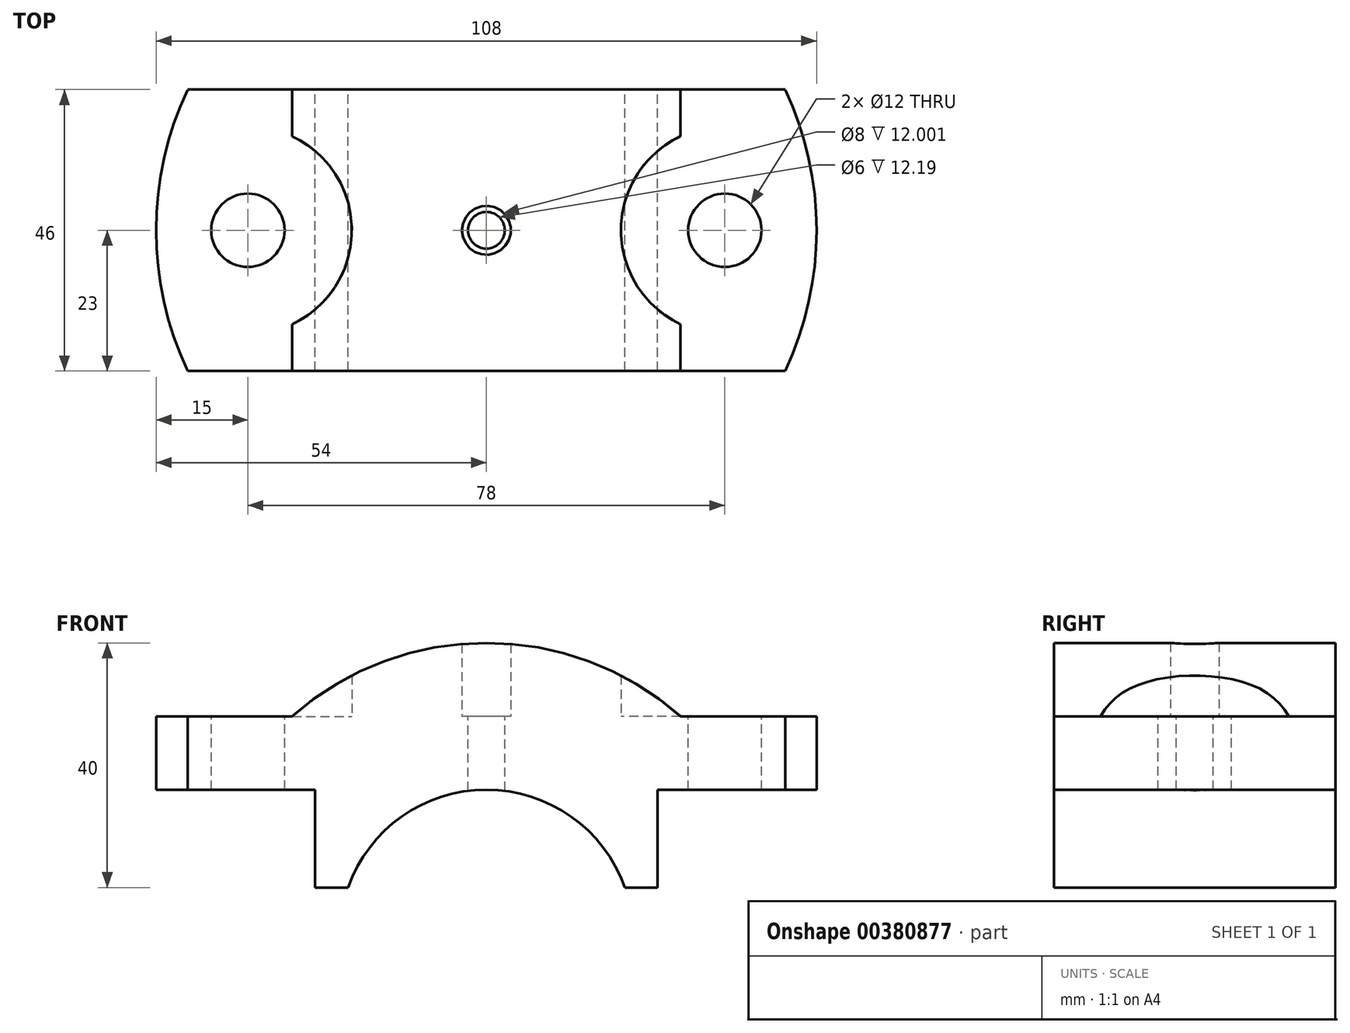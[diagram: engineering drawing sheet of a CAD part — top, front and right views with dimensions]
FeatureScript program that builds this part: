
annotation { "Feature Type Name" : "Feature", "Feature Type Description" : "" }
export const myFeature = defineFeature(function(context is Context, id is Id, definition is map)
    precondition{}
    {
        {
            var Q0;
            Q0=qCreatedBy(makeId("Front.planeOp"),FACE);
            var sketch = newSketch(context, id + "F0", { "sketchPlane" : qUnion([Q0])});
            skLineSegment(sketch, "E0.bottom", {"start": v(-54, 0) * mm, "end": v(54, 0) * mm});
            skLineSegment(sketch, "E0.top", {"start": v(-54, 12) * mm, "end": v(54, 12) * mm});
            skLineSegment(sketch, "E0.left", {"start": v(-54, 0) * mm, "end": v(-54, 12) * mm});
            skLineSegment(sketch, "E0.right", {"start": v(54, 0) * mm, "end": v(54, 12) * mm});
            skSolve(sketch);
        }
        {
            var Q0;
            Q0 = qSketchRegion(id + "F0", true);
            extrude(context, id + "F1", {"entities" : qUnion([Q0]), "endBound" : BoundingType.SYMMETRIC, "depth" : 46 * mm});
        }
        {
            var Q0;
            Q0=qCreatedBy(makeId("Front.planeOp"),FACE);
            var sketch = newSketch(context, id + "F2", { "sketchPlane" : qUnion([Q0])});
            skLineSegment(sketch, "E1", {"start": v(28, 0) * mm, "end": v(28, -16) * mm});
            skLineSegment(sketch, "E2", {"start": v(-28, 0) * mm, "end": v(-28, -16) * mm});
            skArc(sketch, "E3", {"start": v(22.63, -16) * mm, "mid": v(0, 0) * mm, "end": v(-22.63, -16) * mm});
            skLineSegment(sketch, "E4", {"start": v(-28, 0) * mm, "end": v(28, 0) * mm});
            skLineSegment(sketch, "E5", {"start": v(-22.63, -16) * mm, "end": v(-28, -16) * mm});
            skLineSegment(sketch, "E6", {"start": v(22.63, -16) * mm, "end": v(28, -16) * mm});
            skSolve(sketch);
        }
        {
            var Q0;
            Q0 = qSketchRegion(id + "F2", true);
            extrude(context, id + "F3", {"entities" : qUnion([Q0]), "operationType" : NewBodyOperationType.ADD, "endBound" : BoundingType.SYMMETRIC, "depth" : 46 * mm});
        }
        {
            var Q0;
            Q0=qCreatedBy(makeId("Front.planeOp"),FACE);
            var sketch = newSketch(context, id + "F4", { "sketchPlane" : qUnion([Q0])});
            skLineSegment(sketch, "E7.0", {"start": v(-54, 12) * mm, "end": v(54, 12) * mm});
            skArc(sketch, "E8", {"start": v(31.75, 12) * mm, "mid": v(0, 24) * mm, "end": v(-31.75, 12) * mm});
            skSolve(sketch);
        }
        {
            var Q0;
            Q0 = qSketchRegion(id + "F4", true);
            extrude(context, id + "F5", {"entities" : qUnion([Q0]), "operationType" : NewBodyOperationType.ADD, "endBound" : BoundingType.SYMMETRIC, "depth" : 46 * mm});
        }
        {
            var Q0;
            Q0=qCreatedBy(makeId("Top.planeOp"),FACE);
            var sketch = newSketch(context, id + "F6", { "sketchPlane" : qUnion([Q0])});
            skCircle(sketch, "E9", {"center": v(-39, 0) * mm, "radius": 6 * mm});
            skCircle(sketch, "E10", {"center": v(39, 0) * mm, "radius": 6 * mm});
            skSolve(sketch);
        }
        {
            var Q0;
            Q0 = qSketchRegion(id + "F6", true);
            extrude(context, id + "F7", {"entities" : qUnion([Q0]), "operationType" : NewBodyOperationType.REMOVE, "endBound" : BoundingType.THROUGH_ALL, "oppositeDirection" : true, "depth" : 25 * mm, "hasSecondDirection" : true, "secondDirectionOppositeDirection" : false, "secondDirectionDepth" : 25 * mm});
        }
        {
            var Q0;
            {var subQ4=sQuery(id+"F0.wireOp",EDGE,"E0.right");var subQ6=sQuery(id+"F0.wireOp",EDGE,"E0.top");Q0=makeQuery(id+"F5.boolean.opBoolean","SPLIT",FACE,{"disambiguationData":[TD([makeQuery(id+"F1.opExtrude","SWEPT_FACE",FACE,{"disambiguationData":[OSD([subQ4])]})])],"derivedFrom":makeQuery(id+"F1.opExtrude","SWEPT_FACE",FACE,{"disambiguationData":[OSD([subQ6])]})});}
            var sketch = newSketch(context, id + "F8", { "sketchPlane" : qUnion([Q0])});
            skLineSegment(sketch, "E11.0", {"start": v(31.75, -23) * mm, "end": v(31.75, 23) * mm});
            skLineSegment(sketch, "E12.0", {"start": v(-31.75, -23) * mm, "end": v(-31.75, 23) * mm});
            skArc(sketch, "E13", {"start": v(-31.75, -15.38) * mm, "mid": v(-22, 0) * mm, "end": v(-31.75, 15.38) * mm});
            skArc(sketch, "E14", {"start": v(31.75, 15.38) * mm, "mid": v(22, 0) * mm, "end": v(31.75, -15.38) * mm});
            skSolve(sketch);
        }
        {
            var Q0;
            Q0 = qSketchRegion(id + "F8", true);
            extrude(context, id + "F9", {"entities" : qUnion([Q0]), "operationType" : NewBodyOperationType.REMOVE, "depth" : 25 * mm});
        }
        {
            var Q0;
            {var subQ4=sQuery(id+"F0.wireOp",EDGE,"E0.right");var subQ6=sQuery(id+"F0.wireOp",EDGE,"E0.top");Q0=makeQuery(id+"F9.boolean.opBoolean","MERGE",FACE,{"derivedFrom":[makeQuery(id+"F5.boolean.opBoolean","SPLIT",FACE,{"disambiguationData":[TD([makeQuery(id+"F1.opExtrude","SWEPT_FACE",FACE,{"disambiguationData":[OSD([subQ4])]})])],"derivedFrom":makeQuery(id+"F1.opExtrude","SWEPT_FACE",FACE,{"disambiguationData":[OSD([subQ6])]})}),makeQuery(id+"F9.opExtrude","CAP_FACE",FACE,{"disambiguationData":[OSD([sQuery(id+"F8.wireOp",EDGE,"E11.0"),sQuery(id+"F8.wireOp",EDGE,"E14")])],"isStart":true})]});}
            var sketch = newSketch(context, id + "F10", { "sketchPlane" : qUnion([Q0])});
            skCircle(sketch, "E15", {"center": v(0, 0) * mm, "radius": 4 * mm});
            skSolve(sketch);
        }
        {
            var Q0;
            Q0 = qSketchRegion(id + "F10", true);
            extrude(context, id + "F11", {"entities" : qUnion([Q0]), "operationType" : NewBodyOperationType.REMOVE, "depth" : 16 * mm});
        }
        {
            var Q0;
            Q0=makeQuery(id+"F11.boolean.opBoolean","COPY",FACE,{"derivedFrom":makeQuery(id+"F11.opExtrude","CAP_FACE",FACE,{"disambiguationData":[OSD([sQuery(id+"F10.wireOp",EDGE,"E15")])],"isStart":true})});
            var sketch = newSketch(context, id + "F12", { "sketchPlane" : qUnion([Q0])});
            skCircle(sketch, "E16", {"center": v(0, 0) * mm, "radius": 3 * mm});
            skSolve(sketch);
        }
        {
            var Q0;
            Q0 = qSketchRegion(id + "F12", true);
            extrude(context, id + "F13", {"entities" : qUnion([Q0]), "operationType" : NewBodyOperationType.REMOVE, "oppositeDirection" : true, "depth" : 25 * mm, "hasSecondDirection" : true, "secondDirectionOppositeDirection" : false, "secondDirectionDepth" : 25 * mm});
        }
        {
            var Q0;
            {var subQ5=sQuery(id+"F0.wireOp",EDGE,"E0.left");var subQ6=sQuery(id+"F0.wireOp",EDGE,"E0.top");Q0=makeQuery(id+"F9.boolean.opBoolean","MERGE",FACE,{"derivedFrom":[makeQuery(id+"F5.boolean.opBoolean","SPLIT",FACE,{"disambiguationData":[TD([makeQuery(id+"F1.opExtrude","SWEPT_FACE",FACE,{"disambiguationData":[OSD([subQ5])]})])],"derivedFrom":makeQuery(id+"F1.opExtrude","SWEPT_FACE",FACE,{"disambiguationData":[OSD([subQ6])]})}),makeQuery(id+"F9.opExtrude","CAP_FACE",FACE,{"disambiguationData":[OSD([sQuery(id+"F8.wireOp",EDGE,"E12.0"),sQuery(id+"F8.wireOp",EDGE,"E13")])],"isStart":true})]});}
            var sketch = newSketch(context, id + "F14", { "sketchPlane" : qUnion([Q0])});
            skArc(sketch, "E17", {"start": v(-48.86, 23) * mm, "mid": v(-54, 0) * mm, "end": v(-48.86, -23) * mm});
            skLineSegment(sketch, "E18.0", {"start": v(48.86, -23) * mm, "end": v(54, -23) * mm});
            skLineSegment(sketch, "E19.0", {"start": v(48.86, 23) * mm, "end": v(54, 23) * mm});
            skArc(sketch, "E20", {"start": v(48.86, -23) * mm, "mid": v(54, 0) * mm, "end": v(48.86, 23) * mm});
            skPoint(sketch, "E21.orphan", {"position": v(31.75, 23) * mm});
            skLineSegment(sketch, "E22", {"start": v(54, 23) * mm, "end": v(54, -23) * mm});
            skPoint(sketch, "E23.orphan", {"position": v(31.75, -23) * mm});
            skLineSegment(sketch, "E24", {"start": v(-48.86, 23) * mm, "end": v(-54, 23) * mm});
            skLineSegment(sketch, "E25", {"start": v(-54, 23) * mm, "end": v(-54, -23) * mm});
            skLineSegment(sketch, "E26", {"start": v(-54, -23) * mm, "end": v(-48.86, -23) * mm});
            skSolve(sketch);
        }
        {
            var Q0;
            Q0 = qSketchRegion(id + "F14", true);
            extrude(context, id + "F15", {"entities" : qUnion([Q0]), "operationType" : NewBodyOperationType.REMOVE, "oppositeDirection" : true, "depth" : 25 * mm});
        }
    });
